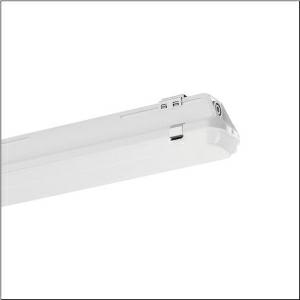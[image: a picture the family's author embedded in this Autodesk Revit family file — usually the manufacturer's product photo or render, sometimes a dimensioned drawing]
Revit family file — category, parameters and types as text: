
# Revit family: monsun_r__11_51fp207p430h_33e7
name_source: partatom
category: Lighting Fixtures
units: mm (PartAtom-declared; Revit-internal decimal feet)

## family parameters
Cut with Voids When Loaded = No
Host = Face
Light Source = No
Part Type = Normal
Room Calculation Point = No
Round Connector Dimension = Use Diameter
Shared = No

## types (1)
- Monsun® 11 (1 x LED, 3990 lm, 24.8 W, 4000K)
    Apparent Load = 25 VA
    CIE Flux Codes = 45 75 93 94 100
    Color Rendering = 80
    Color Temperature = 4000K
    Default Elevation = 1800 mm
    Description = Monsun® 11, damp-proof luminaire, chain hanger, primary optical cover: enclosure, of PC, light emission: direct distribution, primary light characteristic: symmetric, installation type: suspended mounting, surface-mounted, horizontal mounting, vertical mounting, LED, rated luminous flux: 3.990lm, luminous efficacy: 161lm/W, light colour: 840, colour temperature: 4000K, control gear: ON/OFF, with terminal, 3-pole, max. 2.5mm², mains connection: 220..240V, AC, 50/60Hz, rated input power: 25W, luminaire housing, of glass-fibre reinforced polyester, uncoated, bright grey, incl. chain hanger, length: 1.590mm, width: 90mm, height: 88mm, clip for enclosure, of stainless steel (V2A), ceiling mounting element, of stainless steel (V2A), chain hanger, of stainless steel (V2A), protection rating (complete): IP66, insulation class (complete): insulation class I (protective earthing), certification: CE, ENEC, VDE, UKCA, protection symbol: D, impact resistance: IK08, permissible operating ambient temperature: -35..+40°C, standard: EN 50419, EN 60598-2-1, no direct snow, no direct sun, no direct rain, for indoor or canopied outdoor use, corresponds to IFS (International Featured Standards) requirements for safety and quality in the food industry, contact your sales advisor before using the luminaires in applications with unclear chemical exposure, large temperature fluctuations or condensation-forming humidity, LABS conformity tested according to VDMA 24364:2018-05, packaging unit: 1 piece
    Height = 89 mm
    Lamp = 1 x LED
    Lamp Light Flux = 3990 lm
    Lamp Power = 24.8 W
    Lamp count = 1
    Length = 1590 mm
    Luminous efficacy = 161 lm/W
    Manufacturer = Siteco
    ModVariant = No
    Model = 51FP207P430H
    Mounting Place = Ceiling
    Mounting Type = Surface mounted
    Number of Poles = 1
    OnlyDefault = Yes
    Power Factor = 1
    Product Name = Monsun® 11
    Product group = damp-proof luminaire
    ProductGroupID = 300
    Protection Class = Protection class I
    Protection Degree = IP 66
    RLX_Detail_Level = 1
    RLX_Emergency_Light_Flux = 0 lm
    RLX_Emergency_Type = 0
    RLX_Emergency_Type_DB = No
    RlxData = <blob elided: 88749 chars, md5=30b84c5a>
    Socket = socket
    Standby Power = 0 W
    System Light Flux = 3990 lm
    System Power = 25 W
    Type Comments = Product without accessories
    Type Image = l_1349237.jpg
    URL = http://relux.com
    VarID = ---
    Voltage = 0 V
    Weight = 0.00 kg
    Width = 90 mm

## geometry (parser evidence)
native form markers: Blend x4, Sweep x14
no freeform markers — native parametric forms only
